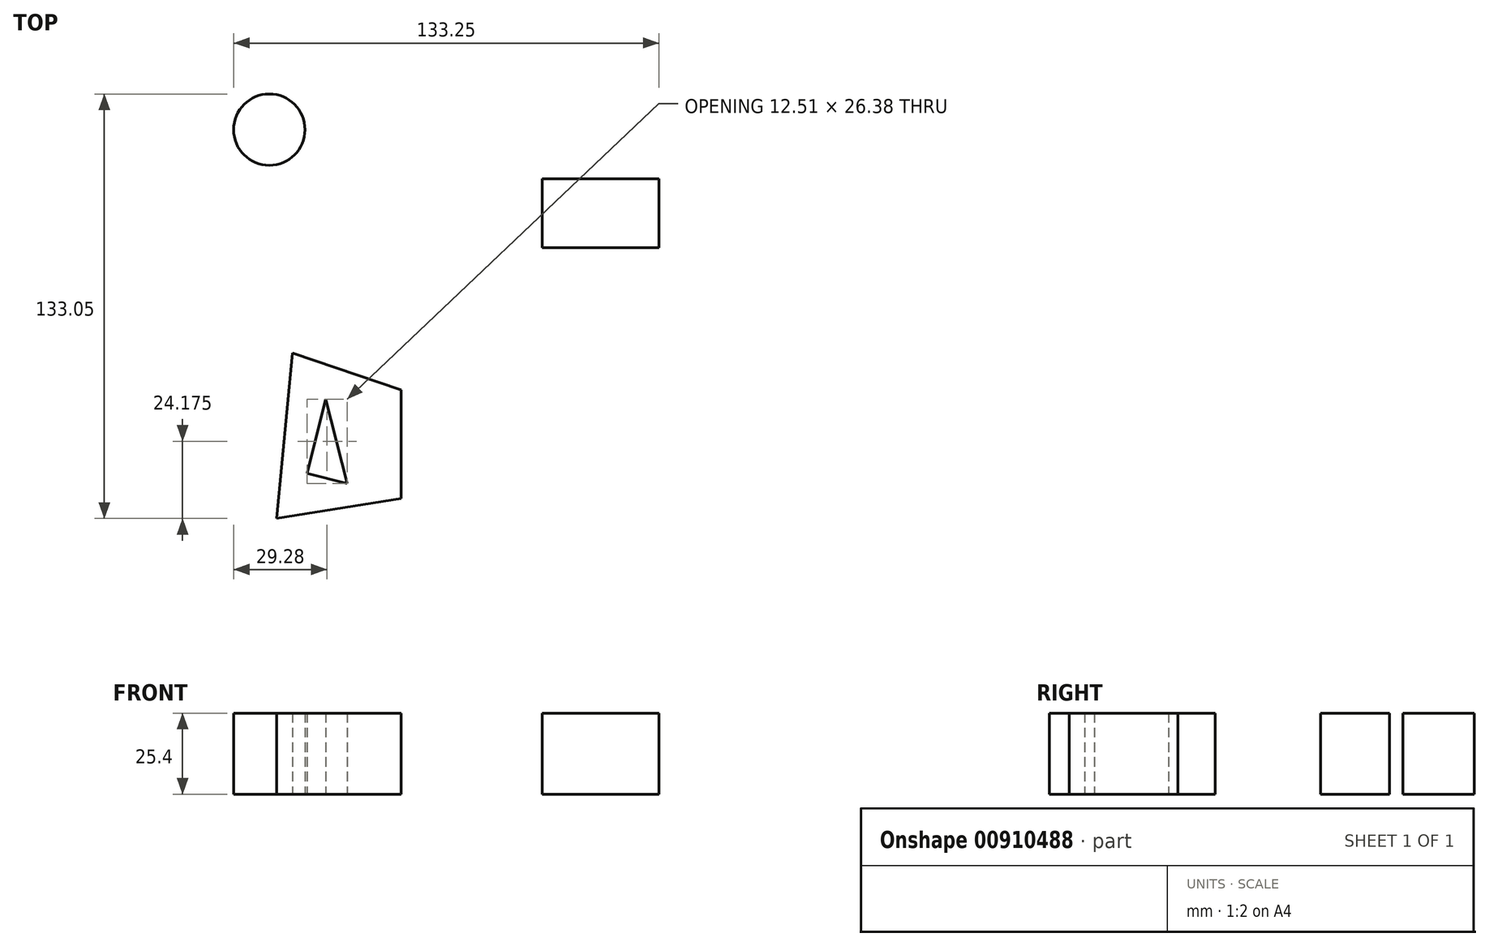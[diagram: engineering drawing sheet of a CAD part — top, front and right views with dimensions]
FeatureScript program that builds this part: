
annotation { "Feature Type Name" : "Feature", "Feature Type Description" : "" }
export const myFeature = defineFeature(function(context is Context, id is Id, definition is map)
    precondition{}
    {
        {
            var Q0;
            Q0=qCreatedBy(makeId("Top.planeOp"),FACE);
            var sketch = newSketch(context, id + "F0", { "sketchPlane" : qUnion([Q0])});
            skCircle(sketch, "E0", {"center": v(-62.28, 52.52) * mm, "radius": 11.18 * mm});
            skLineSegment(sketch, "E1.bottom", {"start": v(23.25, 37.16) * mm, "end": v(59.79, 37.16) * mm});
            skLineSegment(sketch, "E1.top", {"start": v(23.25, 15.57) * mm, "end": v(59.79, 15.57) * mm});
            skLineSegment(sketch, "E1.left", {"start": v(23.25, 37.16) * mm, "end": v(23.25, 15.57) * mm});
            skLineSegment(sketch, "E1.right", {"start": v(59.79, 37.16) * mm, "end": v(59.79, 15.57) * mm});
            skLineSegment(sketch, "E2", {"start": v(-55, -17.45) * mm, "end": v(-20.95, -29.08) * mm});
            skLineSegment(sketch, "E3", {"start": v(-20.95, -29.08) * mm, "end": v(-20.95, -63.13) * mm});
            skLineSegment(sketch, "E4", {"start": v(-20.95, -63.13) * mm, "end": v(-59.98, -69.35) * mm});
            skLineSegment(sketch, "E5", {"start": v(-59.98, -69.35) * mm, "end": v(-55, -17.45) * mm});
            skLineSegment(sketch, "E6", {"start": v(-44.62, -31.99) * mm, "end": v(-50.43, -55.24) * mm});
            skLineSegment(sketch, "E7", {"start": v(-50.43, -55.24) * mm, "end": v(-37.93, -58.36) * mm});
            skLineSegment(sketch, "E8", {"start": v(-37.93, -58.36) * mm, "end": v(-44.62, -31.99) * mm});
            skLineSegment(sketch, "E9", {"start": v(-82.91, 71.7) * mm, "end": v(-82.91, 30.26) * mm, "construction": true});
            skSolve(sketch);
        }
        {
            var Q0;
            Q0=makeQuery(id+"F0.imprint","IMPRINT",FACE,{"disambiguationData":[TD([[makeQuery(id+"F0.imprint","IMPRINT",EDGE,{"derivedFrom":sQuery(id+"F0.wireOp",EDGE,"E2")}),-1.0]])]});
            extrude(context, id + "F1", {"entities" : qUnion([Q0]), "depth" : 25.4 * mm, "offsetDistance" : 25.4 * mm});
        }
        {
            var Q0;
            Q0=makeQuery(id+"F0.imprint","IMPRINT",FACE,{"disambiguationData":[TD([[makeQuery(id+"F0.imprint","IMPRINT",EDGE,{"derivedFrom":sQuery(id+"F0.wireOp",EDGE,"E6")}),1.0]])]});
            var Q1;
            Q1=makeQuery(id+"F0.imprint","IMPRINT",FACE,{"disambiguationData":[TD([[makeQuery(id+"F0.imprint","IMPRINT",EDGE,{"derivedFrom":sQuery(id+"F0.wireOp",EDGE,"E0")}),1.0]])]});
            extrude(context, id + "F2", {"entities" : qUnion([Q0, Q1]), "operationType" : NewBodyOperationType.ADD, "depth" : 25.4 * mm, "offsetDistance" : 25.4 * mm});
        }
        {
            var Q0;
            Q0=makeQuery(id+"F0.imprint","IMPRINT",FACE,{"disambiguationData":[TD([[makeQuery(id+"F0.imprint","IMPRINT",EDGE,{"derivedFrom":sQuery(id+"F0.wireOp",EDGE,"E1.bottom")}),-1.0]])]});
            extrude(context, id + "F3", {"entities" : qUnion([Q0]), "depth" : 25.4 * mm, "offsetDistance" : 25.4 * mm});
        }
        {
            var Q0;
            {var subQ0=sQuery(id+"F0.wireOp",EDGE,"E8");var subQ1=sQuery(id+"F0.wireOp",EDGE,"E7");var subQ2=sQuery(id+"F0.wireOp",EDGE,"E6");Q0=makeQuery(id+"F2.boolean.opBoolean","MERGE",FACE,{"derivedFrom":[makeQuery(id+"F1.opExtrude","CAP_FACE",FACE,{"disambiguationData":[OSD([sQuery(id+"F0.wireOp",EDGE,"E2"),sQuery(id+"F0.wireOp",EDGE,"E3"),sQuery(id+"F0.wireOp",EDGE,"E4"),sQuery(id+"F0.wireOp",EDGE,"E5"),subQ2,subQ1,subQ0])],"isStart":false}),makeQuery(id+"F2.opExtrude","CAP_FACE",FACE,{"disambiguationData":[OSD([subQ2,subQ1,subQ0])],"isStart":false})]});}
            var Q1;
            Q1=makeQuery(id+"F0.imprint","IMPRINT",FACE,{"disambiguationData":[TD([[makeQuery(id+"F0.imprint","IMPRINT",EDGE,{"derivedFrom":sQuery(id+"F0.wireOp",EDGE,"E6")}),1.0]])]});
            extrude(context, id + "F4", {"entities" : qUnion([Q0, Q1]), "operationType" : NewBodyOperationType.REMOVE, "oppositeDirection" : true, "depth" : 25.4 * mm, "offsetDistance" : 25.4 * mm});
        }
        {
            var Q0;
            Q0=makeQuery(id+"F0.imprint","IMPRINT",FACE,{"disambiguationData":[TD([[makeQuery(id+"F0.imprint","IMPRINT",EDGE,{"derivedFrom":sQuery(id+"F0.wireOp",EDGE,"E2")}),-1.0]])]});
            extrude(context, id + "F5", {"entities" : qUnion([Q0]), "depth" : 25.4 * mm, "offsetDistance" : 25.4 * mm});
        }
    });
